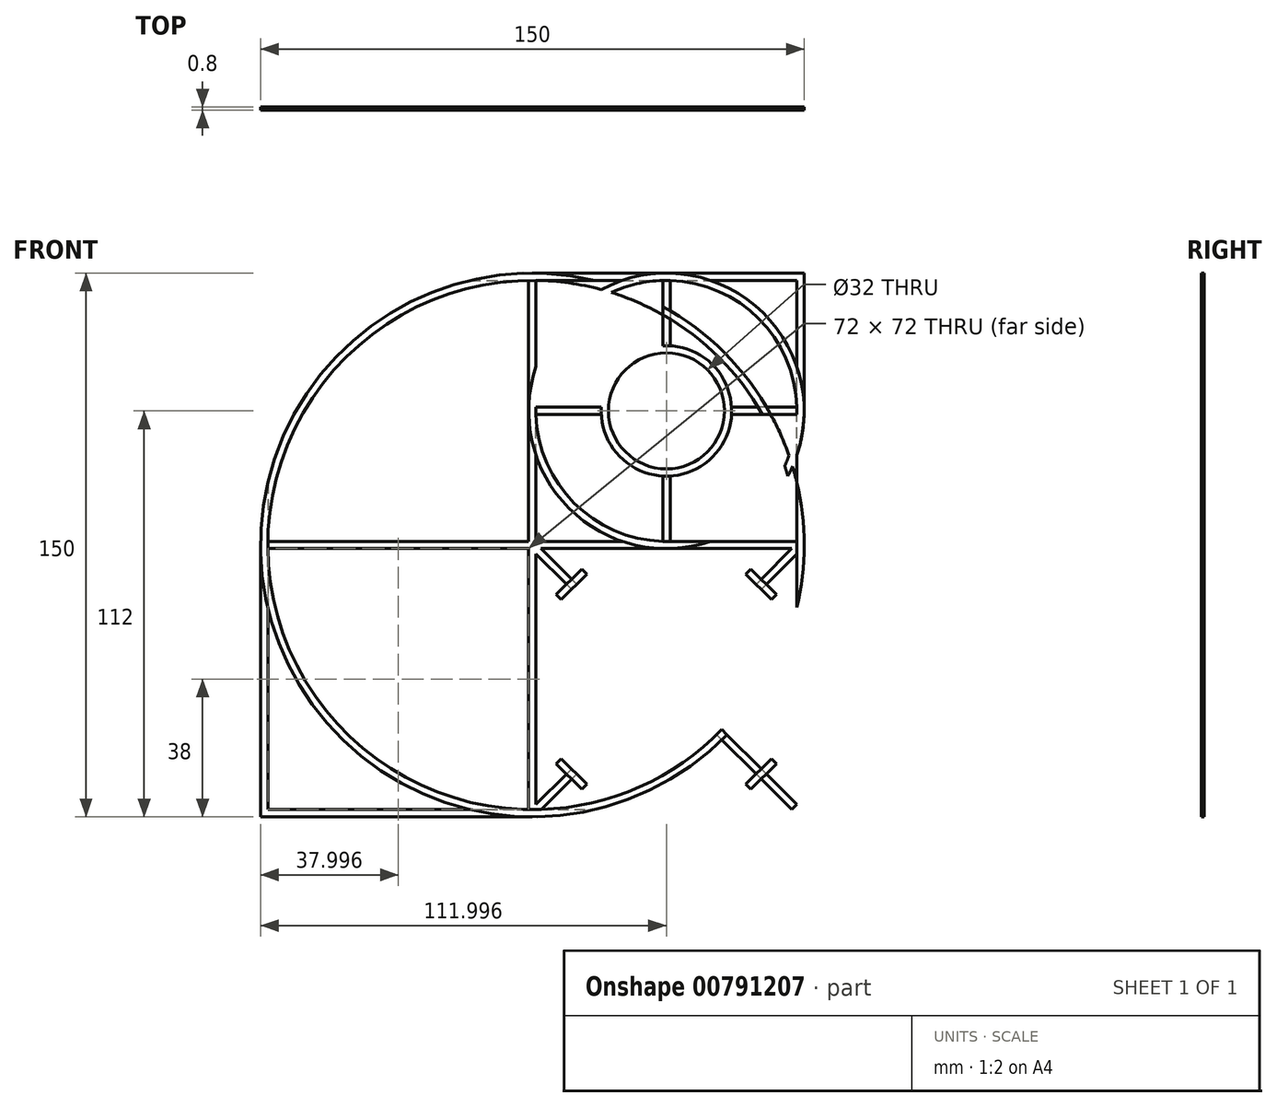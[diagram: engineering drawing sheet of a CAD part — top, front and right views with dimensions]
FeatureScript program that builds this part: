
annotation { "Feature Type Name" : "Feature", "Feature Type Description" : "" }
export const myFeature = defineFeature(function(context is Context, id is Id, definition is map)
    precondition{}
    {
        {
            var Q0;
            Q0=qCreatedBy(makeId("Front.planeOp"),FACE);
            var sketch = newSketch(context, id + "F0", { "sketchPlane" : qUnion([Q0])});
            skLineSegment(sketch, "E0.bottom", {"start": v(-75, 75.04) * mm, "end": v(75, 75.04) * mm});
            skLineSegment(sketch, "E0.top", {"start": v(-75, -74.96) * mm, "end": v(75, -74.96) * mm});
            skLineSegment(sketch, "E0.left", {"start": v(-75, 75.04) * mm, "end": v(-75, -74.96) * mm});
            skLineSegment(sketch, "E0.right", {"start": v(75, 75.04) * mm, "end": v(75, -74.96) * mm});
            skLineSegment(sketch, "E1.bottom", {"start": v(-73, 73.04) * mm, "end": v(-1, 73.04) * mm});
            skLineSegment(sketch, "E1.top", {"start": v(-73, -72.96) * mm, "end": v(-1, -72.96) * mm});
            skLineSegment(sketch, "E1.left", {"start": v(-73, 73.04) * mm, "end": v(-73, 1.04) * mm});
            skLineSegment(sketch, "E2.0", {"start": v(71.6, -0.96) * mm, "end": v(2.42, -0.96) * mm});
            skLineSegment(sketch, "E3.0", {"start": v(-1, 73.04) * mm, "end": v(-1, 1.04) * mm});
            skLineSegment(sketch, "E4.trimOffspring", {"start": v(-73, -0.96) * mm, "end": v(-73, -72.96) * mm});
            skLineSegment(sketch, "E5.trimOffspring", {"start": v(1, -2.37) * mm, "end": v(1, -71.55) * mm});
            skLineSegment(sketch, "E6.trimOffspring", {"start": v(-1, 1.04) * mm, "end": v(-73, 1.04) * mm});
            skLineSegment(sketch, "E7.trimOffspring", {"start": v(-1, -0.96) * mm, "end": v(-1, -72.96) * mm});
            skLineSegment(sketch, "E8.trimOffspring", {"start": v(-1, -0.96) * mm, "end": v(-73, -0.96) * mm});
            skLineSegment(sketch, "E9.trimOffspring", {"start": v(2.42, -72.96) * mm, "end": v(71.6, -72.96) * mm});
            skLineSegment(sketch, "E10.trimOffspring", {"start": v(73, -2.37) * mm, "end": v(73, -71.55) * mm});
            skLineSegment(sketch, "E11.0", {"start": v(1, -2.37) * mm, "end": v(35.6, -36.96) * mm});
            skLineSegment(sketch, "E12.0", {"start": v(2.42, -0.96) * mm, "end": v(37, -35.55) * mm});
            skLineSegment(sketch, "E13.trimOffspring", {"start": v(38.42, -36.96) * mm, "end": v(73, -71.55) * mm});
            skCircle(sketch, "E14", {"center": v(37, 37.04) * mm, "radius": 38 * mm});
            skCircle(sketch, "E15.0", {"center": v(37, 37.04) * mm, "radius": 36 * mm});
            skCircle(sketch, "E16", {"center": v(37, 37.04) * mm, "radius": 18 * mm});
            skCircle(sketch, "E17.0", {"center": v(37, 37.04) * mm, "radius": 16 * mm});
            skLineSegment(sketch, "E18.0", {"start": v(36, 73.04) * mm, "end": v(36, 55.01) * mm});
            skLineSegment(sketch, "E19.0", {"start": v(38, 73.04) * mm, "end": v(38, 55.01) * mm});
            skLineSegment(sketch, "E20.0", {"start": v(73, 38.04) * mm, "end": v(54.98, 38.04) * mm});
            skLineSegment(sketch, "E21.0", {"start": v(73, 36.04) * mm, "end": v(54.98, 36.04) * mm});
            skLineSegment(sketch, "E22.trimOffspring", {"start": v(36, 19.07) * mm, "end": v(36, 1.04) * mm});
            skLineSegment(sketch, "E23.trimOffspring", {"start": v(19.03, 38.04) * mm, "end": v(1, 38.04) * mm});
            skLineSegment(sketch, "E24.trimOffspring", {"start": v(38, 19.07) * mm, "end": v(38, 1.04) * mm});
            skLineSegment(sketch, "E25.trimOffspring", {"start": v(19.03, 36.04) * mm, "end": v(1, 36.04) * mm});
            skText(sketch, "E26", { "text": "36mm OD\n34mm ID", "fontName": "OpenSans-Bold.ttf"});
            skText(sketch, "E27", { "text": "76mm  OD\n72mm  ID", "fontName": "OpenSans-Bold.ttf"});
            skLineSegment(sketch, "E28", {"start": v(71.6, -72.96) * mm, "end": v(37, -38.37) * mm});
            skLineSegment(sketch, "E29", {"start": v(71.6, -0.96) * mm, "end": v(37, -35.55) * mm});
            skLineSegment(sketch, "E30", {"start": v(38.42, -36.96) * mm, "end": v(73, -2.37) * mm});
            skLineSegment(sketch, "E31", {"start": v(1, -71.55) * mm, "end": v(35.6, -36.96) * mm});
            skLineSegment(sketch, "E32", {"start": v(37, -38.37) * mm, "end": v(2.42, -72.96) * mm});
            skLineSegment(sketch, "E33", {"start": v(73, -2.37) * mm, "end": v(71.6, -0.96) * mm});
            skLineSegment(sketch, "E34", {"start": v(1, -71.55) * mm, "end": v(2.42, -72.96) * mm});
            skLineSegment(sketch, "E35", {"start": v(1, -2.37) * mm, "end": v(2.42, -0.96) * mm});
            skLineSegment(sketch, "E36", {"start": v(71.6, -72.96) * mm, "end": v(73, -71.55) * mm});
            skLineSegment(sketch, "E37", {"start": v(37, -35.55) * mm, "end": v(12.26, -10.8) * mm});
            skLineSegment(sketch, "E38", {"start": v(12.26, -10.8) * mm, "end": v(10.84, -12.21) * mm});
            skLineSegment(sketch, "E39", {"start": v(12.26, -10.8) * mm, "end": v(15.09, -7.97) * mm});
            skLineSegment(sketch, "E40", {"start": v(15.09, -7.97) * mm, "end": v(13.67, -6.55) * mm});
            skLineSegment(sketch, "E41", {"start": v(13.67, -6.55) * mm, "end": v(6.6, -13.63) * mm});
            skLineSegment(sketch, "E42", {"start": v(6.6, -13.63) * mm, "end": v(8.01, -15.04) * mm});
            skLineSegment(sketch, "E43", {"start": v(8.01, -15.04) * mm, "end": v(10.84, -12.21) * mm});
            skLineSegment(sketch, "E44", {"start": v(35.6, -36.96) * mm, "end": v(10.84, -61.7) * mm});
            skLineSegment(sketch, "E45", {"start": v(38.42, -36.96) * mm, "end": v(63.17, -61.7) * mm});
            skLineSegment(sketch, "E46", {"start": v(38.42, -36.96) * mm, "end": v(63.17, -12.21) * mm});
            skLineSegment(sketch, "E47", {"start": v(63.17, -12.21) * mm, "end": v(66, -15.04) * mm});
            skLineSegment(sketch, "E48", {"start": v(66, -15.04) * mm, "end": v(67.41, -13.63) * mm});
            skLineSegment(sketch, "E49", {"start": v(67.41, -13.63) * mm, "end": v(60.34, -6.55) * mm});
            skLineSegment(sketch, "E50", {"start": v(60.34, -6.55) * mm, "end": v(58.93, -7.97) * mm});
            skLineSegment(sketch, "E51", {"start": v(58.93, -7.97) * mm, "end": v(63.17, -12.21) * mm});
            skLineSegment(sketch, "E52", {"start": v(10.84, -61.7) * mm, "end": v(8.01, -58.88) * mm});
            skLineSegment(sketch, "E53", {"start": v(8.01, -58.88) * mm, "end": v(6.6, -60.3) * mm});
            skLineSegment(sketch, "E54", {"start": v(6.6, -60.3) * mm, "end": v(13.67, -67.37) * mm});
            skLineSegment(sketch, "E55", {"start": v(13.67, -67.37) * mm, "end": v(15.09, -65.95) * mm});
            skLineSegment(sketch, "E56", {"start": v(15.09, -65.95) * mm, "end": v(10.84, -61.7) * mm});
            skLineSegment(sketch, "E57", {"start": v(63.17, -61.7) * mm, "end": v(66, -58.88) * mm});
            skLineSegment(sketch, "E58", {"start": v(66, -58.88) * mm, "end": v(67.41, -60.3) * mm});
            skLineSegment(sketch, "E59", {"start": v(67.41, -60.3) * mm, "end": v(60.34, -67.37) * mm});
            skLineSegment(sketch, "E60", {"start": v(60.34, -67.37) * mm, "end": v(58.93, -65.95) * mm});
            skLineSegment(sketch, "E61", {"start": v(58.93, -65.95) * mm, "end": v(63.17, -61.7) * mm});
            skLineSegment(sketch, "E62", {"start": v(1, 1.04) * mm, "end": v(1, 73.04) * mm});
            skLineSegment(sketch, "E63", {"start": v(1, 73.04) * mm, "end": v(73, 73.04) * mm});
            skLineSegment(sketch, "E64", {"start": v(1, 1.04) * mm, "end": v(73, 1.04) * mm});
            skLineSegment(sketch, "E65", {"start": v(73, 1.04) * mm, "end": v(73, 73.04) * mm});
            skLineSegment(sketch, "E66", {"start": v(75, 75.04) * mm, "end": v(0, 75.04) * mm});
            skLineSegment(sketch, "E67", {"start": v(75, 75.04) * mm, "end": v(75, 0.04) * mm});
            skLineSegment(sketch, "E68", {"start": v(-75, -74.96) * mm, "end": v(0, -74.96) * mm});
            skCircle(sketch, "E69", {"center": v(0, 0.04) * mm, "radius": 75 * mm});
            skCircle(sketch, "E70.0", {"center": v(0, 0.04) * mm, "radius": 73 * mm});
            skText(sketch, "E71", { "text": "76mm  OD\n72mm  ID", "fontName": "OpenSans-Bold.ttf"});
            const initialGuessF0  = {"E26": [0.02316, 0.03863, 1, 0, 0.00397], "E27": [0.01856, 0.01389, 1, 0, 0.00397], "E71": [0.02468, -0.01252, 1, 0, 0.00397]};
            skSetInitialGuess(sketch, initialGuessF0);
            skSolve(sketch);
        }
        {
            var Q0;
            {var subQ0=sQuery(id+"F0.wireOp",EDGE,"E14");var subQ8=makeQuery(id+"F0.imprint","INTERSECT",VERTEX,{"derivedFrom":[sQuery(id+"F0.wireOp",EDGE,"E1.right"),subQ0]});Q0=makeQuery(id+"F0.imprint","IMPRINT",FACE,{"disambiguationData":[TD([[makeQuery(id+"F0.imprint","IMPRINT",EDGE,{"disambiguationData":[TD([[subQ8,1.0]])],"derivedFrom":subQ0}),1.0]])]});}
            var Q1;
            Q1=makeQuery(id+"F0.imprint","IMPRINT",FACE,{"disambiguationData":[TD([[makeQuery(id+"F0.imprint","IMPRINT",EDGE,{"derivedFrom":sQuery(id+"F0.wireOp",EDGE,"E17.0")}),-1.0]])]});
            var Q2;
            {var subQ0=sQuery(id+"F0.wireOp",EDGE,"E65");var subQ9=sQuery(id+"F0.wireOp",EDGE,"E14");var subQ10=makeQuery(id+"F0.imprint","INTERSECT",VERTEX,{"disambiguationData":[OD(0.0)],"derivedFrom":[subQ9,subQ0]});Q2=makeQuery(id+"F0.imprint","IMPRINT",FACE,{"disambiguationData":[TD([[makeQuery(id+"F0.imprint","IMPRINT",EDGE,{"disambiguationData":[TD([[subQ10,-1.0]])],"derivedFrom":subQ9}),1.0]])]});}
            var Q3;
            {var subQ0=sQuery(id+"F0.wireOp",EDGE,"E63");var subQ9=sQuery(id+"F0.wireOp",EDGE,"E14");var subQ10=makeQuery(id+"F0.imprint","INTERSECT",VERTEX,{"disambiguationData":[OD(1.0)],"derivedFrom":[subQ9,subQ0]});Q3=makeQuery(id+"F0.imprint","IMPRINT",FACE,{"disambiguationData":[TD([[makeQuery(id+"F0.imprint","IMPRINT",EDGE,{"disambiguationData":[TD([[subQ10,-1.0]])],"derivedFrom":subQ9}),1.0]])]});}
            var Q4;
            {var subQ0=sQuery(id+"F0.wireOp",EDGE,"E62");var subQ9=sQuery(id+"F0.wireOp",EDGE,"E14");var subQ10=makeQuery(id+"F0.imprint","INTERSECT",VERTEX,{"disambiguationData":[OD(1.0)],"derivedFrom":[subQ9,subQ0]});Q4=makeQuery(id+"F0.imprint","IMPRINT",FACE,{"disambiguationData":[TD([[makeQuery(id+"F0.imprint","IMPRINT",EDGE,{"disambiguationData":[TD([[subQ10,-1.0]])],"derivedFrom":subQ9}),1.0]])]});}
            var Q5;
            {var subQ0=sQuery(id+"F0.wireOp",EDGE,"E64");var subQ9=sQuery(id+"F0.wireOp",EDGE,"E14");var subQ11=makeQuery(id+"F0.imprint","INTERSECT",VERTEX,{"disambiguationData":[OD(1.0)],"derivedFrom":[subQ9,subQ0]});Q5=makeQuery(id+"F0.imprint","IMPRINT",FACE,{"disambiguationData":[TD([[makeQuery(id+"F0.imprint","IMPRINT",EDGE,{"disambiguationData":[TD([[subQ11,-1.0]])],"derivedFrom":subQ9}),1.0]])]});}
            var Q6;
            {var subQ4=sQuery(id+"F0.wireOp",EDGE,"E42");Q6=makeQuery(id+"F0.imprint","IMPRINT",FACE,{"disambiguationData":[TD([[makeQuery(id+"F0.imprint","IMPRINT",EDGE,{"derivedFrom":subQ4}),1.0]])]});}
            var Q7;
            {var subQ0=sQuery(id+"F0.wireOp",EDGE,"E39");Q7=makeQuery(id+"F0.imprint","IMPRINT",FACE,{"disambiguationData":[TD([[makeQuery(id+"F0.imprint","IMPRINT",EDGE,{"derivedFrom":subQ0}),1.0]])]});}
            var Q8;
            {var subQ0=sQuery(id+"F0.wireOp",EDGE,"E38");Q8=makeQuery(id+"F0.imprint","IMPRINT",FACE,{"disambiguationData":[TD([[makeQuery(id+"F0.imprint","IMPRINT",EDGE,{"derivedFrom":subQ0}),-1.0]])]});}
            var Q9;
            {var subQ0=sQuery(id+"F0.wireOp",EDGE,"E47");Q9=makeQuery(id+"F0.imprint","IMPRINT",FACE,{"disambiguationData":[TD([[makeQuery(id+"F0.imprint","IMPRINT",EDGE,{"derivedFrom":subQ0}),1.0]])]});}
            var Q10;
            {var subQ5=sQuery(id+"F0.wireOp",EDGE,"E50");Q10=makeQuery(id+"F0.imprint","IMPRINT",FACE,{"disambiguationData":[TD([[makeQuery(id+"F0.imprint","IMPRINT",EDGE,{"derivedFrom":subQ5}),1.0]])]});}
            var Q11;
            {var subQ0=sQuery(id+"F0.wireOp",EDGE,"E49");var subQ1=sQuery(id+"F0.wireOp",EDGE,"E29");var subQ2=makeQuery(id+"F0.imprint","INTERSECT",VERTEX,{"derivedFrom":[subQ1,subQ0]});Q11=makeQuery(id+"F0.imprint","IMPRINT",FACE,{"disambiguationData":[TD([[makeQuery(id+"F0.imprint","IMPRINT",EDGE,{"disambiguationData":[TD([[subQ2,-1.0]])],"derivedFrom":subQ1}),1.0]])]});}
            var Q12;
            {var subQ5=sQuery(id+"F0.wireOp",EDGE,"E55");Q12=makeQuery(id+"F0.imprint","IMPRINT",FACE,{"disambiguationData":[TD([[makeQuery(id+"F0.imprint","IMPRINT",EDGE,{"derivedFrom":subQ5}),1.0]])]});}
            var Q13;
            {var subQ0=sQuery(id+"F0.wireOp",EDGE,"E52");Q13=makeQuery(id+"F0.imprint","IMPRINT",FACE,{"disambiguationData":[TD([[makeQuery(id+"F0.imprint","IMPRINT",EDGE,{"derivedFrom":subQ0}),1.0]])]});}
            var Q14;
            {var subQ0=sQuery(id+"F0.wireOp",EDGE,"E56");var subQ5=sQuery(id+"F0.wireOp",EDGE,"E32");var subQ6=makeQuery(id+"F0.imprint","INTERSECT",VERTEX,{"derivedFrom":[subQ5,subQ0]});Q14=makeQuery(id+"F0.imprint","IMPRINT",FACE,{"disambiguationData":[TD([[makeQuery(id+"F0.imprint","IMPRINT",EDGE,{"disambiguationData":[TD([[subQ6,-1.0]])],"derivedFrom":subQ5}),-1.0]])]});}
            var Q15;
            {var subQ3=sQuery(id+"F0.wireOp",EDGE,"E59");var subQ5=sQuery(id+"F0.wireOp",EDGE,"E28");var subQ6=makeQuery(id+"F0.imprint","INTERSECT",VERTEX,{"derivedFrom":[subQ5,subQ3]});Q15=makeQuery(id+"F0.imprint","IMPRINT",FACE,{"disambiguationData":[TD([[makeQuery(id+"F0.imprint","IMPRINT",EDGE,{"disambiguationData":[TD([[subQ6,-1.0]])],"derivedFrom":subQ5}),-1.0]])]});}
            var Q16;
            {var subQ0=sQuery(id+"F0.wireOp",EDGE,"E57");Q16=makeQuery(id+"F0.imprint","IMPRINT",FACE,{"disambiguationData":[TD([[makeQuery(id+"F0.imprint","IMPRINT",EDGE,{"derivedFrom":subQ0}),-1.0]])]});}
            var Q17;
            {var subQ5=sQuery(id+"F0.wireOp",EDGE,"E60");Q17=makeQuery(id+"F0.imprint","IMPRINT",FACE,{"disambiguationData":[TD([[makeQuery(id+"F0.imprint","IMPRINT",EDGE,{"derivedFrom":subQ5}),-1.0]])]});}
            var Q18;
            {var subQ3=sQuery(id+"F0.wireOp",EDGE,"E14");var subQ7=sQuery(id+"F0.wireOp",EDGE,"E70.0");var subQ9=makeQuery(id+"F0.imprint","INTERSECT",VERTEX,{"disambiguationData":[OD(0.0)],"derivedFrom":[subQ3,subQ7]});Q18=makeQuery(id+"F0.imprint","IMPRINT",FACE,{"disambiguationData":[TD([[makeQuery(id+"F0.imprint","IMPRINT",EDGE,{"disambiguationData":[TD([[subQ9,-1.0]])],"derivedFrom":subQ3}),1.0]])]});}
            var Q19;
            {var subQ0=sQuery(id+"F0.wireOp",EDGE,"E69");var subQ1=sQuery(id+"F0.wireOp",EDGE,"E14");var subQ2=makeQuery(id+"F0.imprint","INTERSECT",VERTEX,{"disambiguationData":[OD(0.0)],"derivedFrom":[subQ1,subQ0]});Q19=makeQuery(id+"F0.imprint","IMPRINT",FACE,{"disambiguationData":[TD([[makeQuery(id+"F0.imprint","IMPRINT",EDGE,{"disambiguationData":[TD([[subQ2,-1.0]])],"derivedFrom":subQ1}),-1.0]])]});}
            var Q20;
            {var subQ0=sQuery(id+"F0.wireOp",EDGE,"E69");var subQ1=sQuery(id+"F0.wireOp",EDGE,"E15.0");var subQ2=makeQuery(id+"F0.imprint","INTERSECT",VERTEX,{"disambiguationData":[OD(0.0)],"derivedFrom":[subQ1,subQ0]});Q20=makeQuery(id+"F0.imprint","IMPRINT",FACE,{"disambiguationData":[TD([[makeQuery(id+"F0.imprint","IMPRINT",EDGE,{"disambiguationData":[TD([[subQ2,-1.0]])],"derivedFrom":subQ1}),1.0]])]});}
            var Q21;
            {var subQ0=sQuery(id+"F0.wireOp",EDGE,"E69");var subQ1=sQuery(id+"F0.wireOp",EDGE,"E18.0");var subQ2=makeQuery(id+"F0.imprint","INTERSECT",VERTEX,{"derivedFrom":[subQ1,subQ0]});Q21=makeQuery(id+"F0.imprint","IMPRINT",FACE,{"disambiguationData":[TD([[makeQuery(id+"F0.imprint","IMPRINT",EDGE,{"disambiguationData":[TD([[subQ2,-1.0]])],"derivedFrom":subQ1}),1.0]])]});}
            var Q22;
            {var subQ0=sQuery(id+"F0.wireOp",EDGE,"E69");var subQ1=sQuery(id+"F0.wireOp",EDGE,"E19.0");var subQ2=makeQuery(id+"F0.imprint","INTERSECT",VERTEX,{"derivedFrom":[subQ1,subQ0]});Q22=makeQuery(id+"F0.imprint","IMPRINT",FACE,{"disambiguationData":[TD([[makeQuery(id+"F0.imprint","IMPRINT",EDGE,{"disambiguationData":[TD([[subQ2,-1.0]])],"derivedFrom":subQ1}),1.0]])]});}
            var Q23;
            {var subQ0=sQuery(id+"F0.wireOp",EDGE,"E70.0");var subQ1=sQuery(id+"F0.wireOp",EDGE,"E15.0");var subQ2=makeQuery(id+"F0.imprint","INTERSECT",VERTEX,{"disambiguationData":[OD(1.0)],"derivedFrom":[subQ1,subQ0]});Q23=makeQuery(id+"F0.imprint","IMPRINT",FACE,{"disambiguationData":[TD([[makeQuery(id+"F0.imprint","IMPRINT",EDGE,{"disambiguationData":[TD([[subQ2,-1.0]])],"derivedFrom":subQ1}),1.0]])]});}
            var Q24;
            {var subQ0=sQuery(id+"F0.wireOp",EDGE,"E69");var subQ1=sQuery(id+"F0.wireOp",EDGE,"E20.0");var subQ2=makeQuery(id+"F0.imprint","INTERSECT",VERTEX,{"derivedFrom":[subQ1,subQ0]});Q24=makeQuery(id+"F0.imprint","IMPRINT",FACE,{"disambiguationData":[TD([[makeQuery(id+"F0.imprint","IMPRINT",EDGE,{"disambiguationData":[TD([[subQ2,-1.0]])],"derivedFrom":subQ1}),1.0]])]});}
            var Q25;
            {var subQ0=sQuery(id+"F0.wireOp",EDGE,"E70.0");var subQ1=sQuery(id+"F0.wireOp",EDGE,"E14");var subQ2=makeQuery(id+"F0.imprint","INTERSECT",VERTEX,{"disambiguationData":[OD(1.0)],"derivedFrom":[subQ1,subQ0]});Q25=makeQuery(id+"F0.imprint","IMPRINT",FACE,{"disambiguationData":[TD([[makeQuery(id+"F0.imprint","IMPRINT",EDGE,{"disambiguationData":[TD([[subQ2,-1.0]])],"derivedFrom":subQ1}),1.0]])]});}
            var Q26;
            {var subQ5=sQuery(id+"F0.wireOp",EDGE,"E70.0");var subQ7=sQuery(id+"F0.wireOp",EDGE,"E14");var subQ9=makeQuery(id+"F0.imprint","INTERSECT",VERTEX,{"disambiguationData":[OD(1.0)],"derivedFrom":[subQ7,subQ5]});Q26=makeQuery(id+"F0.imprint","IMPRINT",FACE,{"disambiguationData":[TD([[makeQuery(id+"F0.imprint","IMPRINT",EDGE,{"disambiguationData":[TD([[subQ9,-1.0]])],"derivedFrom":subQ7}),-1.0]])]});}
            var Q27;
            {var subQ3=sQuery(id+"F0.wireOp",EDGE,"E45");var subQ5=sQuery(id+"F0.wireOp",EDGE,"E70.0");var subQ6=makeQuery(id+"F0.imprint","INTERSECT",VERTEX,{"derivedFrom":[subQ3,subQ5]});Q27=makeQuery(id+"F0.imprint","IMPRINT",FACE,{"disambiguationData":[TD([[makeQuery(id+"F0.imprint","IMPRINT",EDGE,{"disambiguationData":[TD([[subQ6,-1.0]])],"derivedFrom":subQ3}),1.0]])]});}
            var Q28;
            {var subQ0=sQuery(id+"F0.wireOp",EDGE,"E65");var subQ1=sQuery(id+"F0.wireOp",EDGE,"E64");var subQ2=makeQuery(id+"F0.imprint","INTERSECT",VERTEX,{"derivedFrom":[subQ1,subQ0]});Q28=makeQuery(id+"F0.imprint","IMPRINT",FACE,{"disambiguationData":[TD([[makeQuery(id+"F0.imprint","IMPRINT",EDGE,{"disambiguationData":[TD([[subQ2,1.0]])],"derivedFrom":subQ1}),-1.0]])]});}
            var Q29;
            {var subQ0=sQuery(id+"F0.wireOp",EDGE,"E69");var subQ3=sQuery(id+"F0.wireOp",EDGE,"E28");var subQ4=makeQuery(id+"F0.imprint","INTERSECT",VERTEX,{"derivedFrom":[subQ3,subQ0]});Q29=makeQuery(id+"F0.imprint","IMPRINT",FACE,{"disambiguationData":[TD([[makeQuery(id+"F0.imprint","IMPRINT",EDGE,{"disambiguationData":[TD([[subQ4,-1.0]])],"derivedFrom":subQ3}),1.0]])]});}
            var Q30;
            {var subQ0=sQuery(id+"F0.wireOp",EDGE,"E69");var subQ1=sQuery(id+"F0.wireOp",EDGE,"E28");var subQ2=makeQuery(id+"F0.imprint","INTERSECT",VERTEX,{"derivedFrom":[subQ1,subQ0]});Q30=makeQuery(id+"F0.imprint","IMPRINT",FACE,{"disambiguationData":[TD([[makeQuery(id+"F0.imprint","IMPRINT",EDGE,{"disambiguationData":[TD([[subQ2,-1.0]])],"derivedFrom":subQ1}),-1.0]])]});}
            var Q31;
            {var subQ5=sQuery(id+"F0.wireOp",EDGE,"E7.trimOffspring");var subQ6=sQuery(id+"F0.wireOp",EDGE,"E1.top");var subQ7=makeQuery(id+"F0.imprint","INTERSECT",VERTEX,{"derivedFrom":[subQ6,subQ5]});Q31=makeQuery(id+"F0.imprint","IMPRINT",FACE,{"disambiguationData":[TD([[makeQuery(id+"F0.imprint","IMPRINT",EDGE,{"disambiguationData":[TD([[subQ7,1.0]])],"derivedFrom":subQ6}),1.0]])]});}
            var Q32;
            {var subQ7=sQuery(id+"F0.wireOp",EDGE,"E7.trimOffspring");var subQ8=sQuery(id+"F0.wireOp",EDGE,"E1.top");var subQ9=makeQuery(id+"F0.imprint","INTERSECT",VERTEX,{"derivedFrom":[subQ8,subQ7]});Q32=makeQuery(id+"F0.imprint","IMPRINT",FACE,{"disambiguationData":[TD([[makeQuery(id+"F0.imprint","IMPRINT",EDGE,{"disambiguationData":[TD([[subQ9,1.0]])],"derivedFrom":subQ8}),-1.0]])]});}
            var Q33;
            {var subQ0=sQuery(id+"F0.wireOp",EDGE,"E3.0");var subQ1=sQuery(id+"F0.wireOp",EDGE,"E1.bottom");var subQ2=makeQuery(id+"F0.imprint","INTERSECT",VERTEX,{"derivedFrom":[subQ1,subQ0]});Q33=makeQuery(id+"F0.imprint","IMPRINT",FACE,{"disambiguationData":[TD([[makeQuery(id+"F0.imprint","IMPRINT",EDGE,{"disambiguationData":[TD([[subQ2,1.0]])],"derivedFrom":subQ1}),-1.0]])]});}
            var Q34;
            {var subQ8=sQuery(id+"F0.wireOp",EDGE,"E1.left");var subQ10=sQuery(id+"F0.wireOp",EDGE,"E6.trimOffspring");var subQ11=makeQuery(id+"F0.imprint","INTERSECT",VERTEX,{"derivedFrom":[subQ8,subQ10]});Q34=makeQuery(id+"F0.imprint","IMPRINT",FACE,{"disambiguationData":[TD([[makeQuery(id+"F0.imprint","IMPRINT",EDGE,{"disambiguationData":[TD([[subQ11,1.0]])],"derivedFrom":subQ8}),-1.0]])]});}
            var Q35;
            {var subQ5=sQuery(id+"F0.wireOp",EDGE,"E3.0");var subQ6=sQuery(id+"F0.wireOp",EDGE,"E1.bottom");var subQ7=makeQuery(id+"F0.imprint","INTERSECT",VERTEX,{"derivedFrom":[subQ6,subQ5]});Q35=makeQuery(id+"F0.imprint","IMPRINT",FACE,{"disambiguationData":[TD([[makeQuery(id+"F0.imprint","IMPRINT",EDGE,{"disambiguationData":[TD([[subQ7,1.0]])],"derivedFrom":subQ6}),1.0]])]});}
            var Q36;
            {var subQ0=sQuery(id+"F0.wireOp",EDGE,"E69");var subQ1=sQuery(id+"F0.wireOp",EDGE,"E14");var subQ2=makeQuery(id+"F0.imprint","INTERSECT",VERTEX,{"disambiguationData":[OD(0.0)],"derivedFrom":[subQ1,subQ0]});Q36=makeQuery(id+"F0.imprint","IMPRINT",FACE,{"disambiguationData":[TD([[makeQuery(id+"F0.imprint","IMPRINT",EDGE,{"disambiguationData":[TD([[subQ2,-1.0]])],"derivedFrom":subQ1}),1.0]])]});}
            var Q37;
            {var subQ3=sQuery(id+"F0.wireOp",EDGE,"E14");var subQ7=sQuery(id+"F0.wireOp",EDGE,"E69");var subQ9=makeQuery(id+"F0.imprint","INTERSECT",VERTEX,{"disambiguationData":[OD(1.0)],"derivedFrom":[subQ3,subQ7]});Q37=makeQuery(id+"F0.imprint","IMPRINT",FACE,{"disambiguationData":[TD([[makeQuery(id+"F0.imprint","IMPRINT",EDGE,{"disambiguationData":[TD([[subQ9,-1.0]])],"derivedFrom":subQ3}),1.0]])]});}
            extrude(context, id + "F1", {"entities" : qUnion([Q0, Q1, Q2, Q3, Q4, Q5, Q6, Q7, Q8, Q9, Q10, Q11, Q12, Q13, Q14, Q15, Q16, Q17, Q18, Q19, Q20, Q21, Q22, Q23, Q24, Q25, Q26, Q27, Q28, Q29, Q30, Q31, Q32, Q33, Q34, Q35, Q36, Q37]), "depth" : .8 * mm, "offsetDistance" : 25 * mm});
        }
        {
            var Q0;
            {var subQ7=sQuery(id+"F0.wireOp",EDGE,"E0.top");Q0=makeQuery(id+"F0.imprint","IMPRINT",FACE,{"disambiguationData":[TD([[makeQuery(id+"F0.imprint","IMPRINT",EDGE,{"derivedFrom":subQ7}),1.0]])]});}
            var Q1;
            {var subQ6=sQuery(id+"F0.wireOp",EDGE,"E0.bottom");Q1=makeQuery(id+"F0.imprint","IMPRINT",FACE,{"disambiguationData":[TD([[makeQuery(id+"F0.imprint","IMPRINT",EDGE,{"derivedFrom":subQ6}),-1.0]])]});}
            var Q2;
            {var subQ0=sQuery(id+"F0.wireOp",EDGE,"E23.trimOffspring");var subQ5=sQuery(id+"F0.wireOp",EDGE,"E15.0");var subQ8=makeQuery(id+"F0.imprint","INTERSECT",VERTEX,{"derivedFrom":[subQ5,subQ0]});Q2=makeQuery(id+"F0.imprint","IMPRINT",FACE,{"disambiguationData":[TD([[makeQuery(id+"F0.imprint","IMPRINT",EDGE,{"disambiguationData":[TD([[subQ8,-1.0]])],"derivedFrom":subQ5}),1.0]])]});}
            var Q3;
            {var subQ0=sQuery(id+"F0.wireOp",EDGE,"E22.trimOffspring");var subQ3=sQuery(id+"F0.wireOp",EDGE,"E15.0");var subQ4=makeQuery(id+"F0.imprint","INTERSECT",VERTEX,{"derivedFrom":[subQ3,subQ0]});Q3=makeQuery(id+"F0.imprint","IMPRINT",FACE,{"disambiguationData":[TD([[makeQuery(id+"F0.imprint","IMPRINT",EDGE,{"disambiguationData":[TD([[subQ4,-1.0]])],"derivedFrom":subQ3}),1.0]])]});}
            var Q4;
            {var subQ0=sQuery(id+"F0.wireOp",EDGE,"E19.0");var subQ1=sQuery(id+"F0.wireOp",EDGE,"E15.0");var subQ2=makeQuery(id+"F0.imprint","INTERSECT",VERTEX,{"derivedFrom":[subQ1,subQ0]});Q4=makeQuery(id+"F0.imprint","IMPRINT",FACE,{"disambiguationData":[TD([[makeQuery(id+"F0.imprint","IMPRINT",EDGE,{"disambiguationData":[TD([[subQ2,-1.0]])],"derivedFrom":subQ1}),1.0]])]});}
            var Q5;
            {var subQ1=sQuery(id+"F0.wireOp",EDGE,"E15.0");var subQ5=sQuery(id+"F0.wireOp",EDGE,"E20.0");var subQ6=makeQuery(id+"F0.imprint","INTERSECT",VERTEX,{"derivedFrom":[subQ1,subQ5]});Q5=makeQuery(id+"F0.imprint","IMPRINT",FACE,{"disambiguationData":[TD([[makeQuery(id+"F0.imprint","IMPRINT",EDGE,{"disambiguationData":[TD([[subQ6,1.0]])],"derivedFrom":subQ1}),1.0]])]});}
            var Q6;
            {var subQ0=sQuery(id+"F0.wireOp",EDGE,"E35");Q6=makeQuery(id+"F0.imprint","IMPRINT",FACE,{"disambiguationData":[TD([[makeQuery(id+"F0.imprint","IMPRINT",EDGE,{"derivedFrom":subQ0}),-1.0]])]});}
            var Q7;
            {var subQ13=sQuery(id+"F0.wireOp",EDGE,"E37");Q7=makeQuery(id+"F0.imprint","IMPRINT",FACE,{"disambiguationData":[TD([[makeQuery(id+"F0.imprint","IMPRINT",EDGE,{"derivedFrom":subQ13}),1.0]])]});}
            var Q8;
            {var subQ1=sQuery(id+"F0.wireOp",EDGE,"E30");var subQ3=sQuery(id+"F0.wireOp",EDGE,"E70.0");var subQ4=makeQuery(id+"F0.imprint","INTERSECT",VERTEX,{"derivedFrom":[subQ1,subQ3]});Q8=makeQuery(id+"F0.imprint","IMPRINT",FACE,{"disambiguationData":[TD([[makeQuery(id+"F0.imprint","IMPRINT",EDGE,{"disambiguationData":[TD([[subQ4,-1.0]])],"derivedFrom":subQ3}),-1.0]])]});}
            var Q9;
            {var subQ0=sQuery(id+"F0.wireOp",EDGE,"E36");Q9=makeQuery(id+"F0.imprint","IMPRINT",FACE,{"disambiguationData":[TD([[makeQuery(id+"F0.imprint","IMPRINT",EDGE,{"derivedFrom":subQ0}),1.0]])]});}
            var Q10;
            {var subQ1=sQuery(id+"F0.wireOp",EDGE,"E32");var subQ3=sQuery(id+"F0.wireOp",EDGE,"E70.0");var subQ4=makeQuery(id+"F0.imprint","INTERSECT",VERTEX,{"derivedFrom":[subQ1,subQ3]});Q10=makeQuery(id+"F0.imprint","IMPRINT",FACE,{"disambiguationData":[TD([[makeQuery(id+"F0.imprint","IMPRINT",EDGE,{"disambiguationData":[TD([[subQ4,1.0]])],"derivedFrom":subQ3}),-1.0]])]});}
            var Q11;
            {var subQ0=sQuery(id+"F0.wireOp",EDGE,"E61");var subQ1=sQuery(id+"F0.wireOp",EDGE,"E28");var subQ2=makeQuery(id+"F0.imprint","INTERSECT",VERTEX,{"derivedFrom":[subQ1,subQ0]});Q11=makeQuery(id+"F0.imprint","IMPRINT",FACE,{"disambiguationData":[TD([[makeQuery(id+"F0.imprint","IMPRINT",EDGE,{"disambiguationData":[TD([[subQ2,-1.0]])],"derivedFrom":subQ1}),-1.0]])]});}
            var Q12;
            {var subQ0=sQuery(id+"F0.wireOp",EDGE,"E69");var subQ1=sQuery(id+"F0.wireOp",EDGE,"E28");var subQ2=makeQuery(id+"F0.imprint","INTERSECT",VERTEX,{"derivedFrom":[subQ1,subQ0]});Q12=makeQuery(id+"F0.imprint","IMPRINT",FACE,{"disambiguationData":[TD([[makeQuery(id+"F0.imprint","IMPRINT",EDGE,{"disambiguationData":[TD([[subQ2,-1.0]])],"derivedFrom":subQ1}),-1.0]])]});}
            var Q13;
            {var subQ0=sQuery(id+"F0.wireOp",EDGE,"E20.0");var subQ1=sQuery(id+"F0.wireOp",EDGE,"E16");var subQ2=makeQuery(id+"F0.imprint","INTERSECT",VERTEX,{"derivedFrom":[subQ1,subQ0]});Q13=makeQuery(id+"F0.imprint","IMPRINT",FACE,{"disambiguationData":[TD([[makeQuery(id+"F0.imprint","IMPRINT",EDGE,{"disambiguationData":[TD([[subQ2,1.0]])],"derivedFrom":subQ1}),-1.0]])]});}
            var Q14;
            {var subQ0=sQuery(id+"F0.wireOp",EDGE,"E69");var subQ1=sQuery(id+"F0.wireOp",EDGE,"E20.0");var subQ2=makeQuery(id+"F0.imprint","INTERSECT",VERTEX,{"derivedFrom":[subQ1,subQ0]});Q14=makeQuery(id+"F0.imprint","IMPRINT",FACE,{"disambiguationData":[TD([[makeQuery(id+"F0.imprint","IMPRINT",EDGE,{"disambiguationData":[TD([[subQ2,-1.0]])],"derivedFrom":subQ1}),1.0]])]});}
            var Q15;
            {var subQ0=sQuery(id+"F0.wireOp",EDGE,"E69");var subQ1=sQuery(id+"F0.wireOp",EDGE,"E18.0");var subQ2=makeQuery(id+"F0.imprint","INTERSECT",VERTEX,{"derivedFrom":[subQ1,subQ0]});Q15=makeQuery(id+"F0.imprint","IMPRINT",FACE,{"disambiguationData":[TD([[makeQuery(id+"F0.imprint","IMPRINT",EDGE,{"disambiguationData":[TD([[subQ2,-1.0]])],"derivedFrom":subQ1}),1.0]])]});}
            var Q16;
            {var subQ0=sQuery(id+"F0.wireOp",EDGE,"E18.0");var subQ1=sQuery(id+"F0.wireOp",EDGE,"E16");var subQ2=makeQuery(id+"F0.imprint","INTERSECT",VERTEX,{"derivedFrom":[subQ1,subQ0]});Q16=makeQuery(id+"F0.imprint","IMPRINT",FACE,{"disambiguationData":[TD([[makeQuery(id+"F0.imprint","IMPRINT",EDGE,{"disambiguationData":[TD([[subQ2,1.0]])],"derivedFrom":subQ1}),-1.0]])]});}
            var Q17;
            {var subQ0=sQuery(id+"F0.wireOp",EDGE,"E66");var subQ1=sQuery(id+"F0.wireOp",EDGE,"E14");var subQ2=makeQuery(id+"F0.imprint","INTERSECT",VERTEX,{"derivedFrom":[subQ1,subQ0]});Q17=makeQuery(id+"F0.imprint","IMPRINT",FACE,{"disambiguationData":[TD([[makeQuery(id+"F0.imprint","IMPRINT",EDGE,{"disambiguationData":[TD([[subQ2,-1.0]])],"derivedFrom":subQ1}),-1.0]])]});}
            var Q18;
            {var subQ3=sQuery(id+"F0.wireOp",EDGE,"E14");var subQ8=sQuery(id+"F0.wireOp",EDGE,"E67");var subQ9=makeQuery(id+"F0.imprint","INTERSECT",VERTEX,{"derivedFrom":[subQ3,subQ8]});Q18=makeQuery(id+"F0.imprint","IMPRINT",FACE,{"disambiguationData":[TD([[makeQuery(id+"F0.imprint","IMPRINT",EDGE,{"disambiguationData":[TD([[subQ9,-1.0]])],"derivedFrom":subQ3}),-1.0]])]});}
            var Q19;
            {var subQ0=sQuery(id+"F0.wireOp",EDGE,"E67");var subQ1=sQuery(id+"F0.wireOp",EDGE,"E14");var subQ2=makeQuery(id+"F0.imprint","INTERSECT",VERTEX,{"derivedFrom":[subQ1,subQ0]});Q19=makeQuery(id+"F0.imprint","IMPRINT",FACE,{"disambiguationData":[TD([[makeQuery(id+"F0.imprint","IMPRINT",EDGE,{"disambiguationData":[TD([[subQ2,1.0]])],"derivedFrom":subQ1}),-1.0]])]});}
            var Q20;
            {var subQ0=sQuery(id+"F0.wireOp",EDGE,"E65");var subQ1=sQuery(id+"F0.wireOp",EDGE,"E64");var subQ2=makeQuery(id+"F0.imprint","INTERSECT",VERTEX,{"derivedFrom":[subQ1,subQ0]});Q20=makeQuery(id+"F0.imprint","IMPRINT",FACE,{"disambiguationData":[TD([[makeQuery(id+"F0.imprint","IMPRINT",EDGE,{"disambiguationData":[TD([[subQ2,1.0]])],"derivedFrom":subQ1}),-1.0]])]});}
            var Q21;
            {var subQ3=sQuery(id+"F0.wireOp",EDGE,"E14");var subQ5=makeQuery(id+"F0.imprint","INTERSECT",VERTEX,{"derivedFrom":[subQ3,sQuery(id+"F0.wireOp",EDGE,"E67")]});Q21=makeQuery(id+"F0.imprint","IMPRINT",FACE,{"disambiguationData":[TD([[makeQuery(id+"F0.imprint","IMPRINT",EDGE,{"disambiguationData":[TD([[subQ5,-1.0]])],"derivedFrom":subQ3}),1.0]])]});}
            var Q22;
            {var subQ3=sQuery(id+"F0.wireOp",EDGE,"E14");var subQ5=makeQuery(id+"F0.imprint","INTERSECT",VERTEX,{"derivedFrom":[subQ3,sQuery(id+"F0.wireOp",EDGE,"E66")]});Q22=makeQuery(id+"F0.imprint","IMPRINT",FACE,{"disambiguationData":[TD([[makeQuery(id+"F0.imprint","IMPRINT",EDGE,{"disambiguationData":[TD([[subQ5,1.0]])],"derivedFrom":subQ3}),1.0]])]});}
            var Q23;
            {var subQ5=sQuery(id+"F0.wireOp",EDGE,"E3.0");var subQ6=sQuery(id+"F0.wireOp",EDGE,"E1.bottom");var subQ7=makeQuery(id+"F0.imprint","INTERSECT",VERTEX,{"derivedFrom":[subQ6,subQ5]});Q23=makeQuery(id+"F0.imprint","IMPRINT",FACE,{"disambiguationData":[TD([[makeQuery(id+"F0.imprint","IMPRINT",EDGE,{"disambiguationData":[TD([[subQ7,1.0]])],"derivedFrom":subQ6}),1.0]])]});}
            var Q24;
            {var subQ0=sQuery(id+"F0.wireOp",EDGE,"E70.0");var subQ1=sQuery(id+"F0.wireOp",EDGE,"E3.0");var subQ2=makeQuery(id+"F0.imprint","INTERSECT",VERTEX,{"derivedFrom":[subQ1,subQ0]});Q24=makeQuery(id+"F0.imprint","IMPRINT",FACE,{"disambiguationData":[TD([[makeQuery(id+"F0.imprint","IMPRINT",EDGE,{"disambiguationData":[TD([[subQ2,-1.0]])],"derivedFrom":subQ1}),1.0]])]});}
            var Q25;
            {var subQ3=sQuery(id+"F0.wireOp",EDGE,"E14");var subQ5=makeQuery(id+"F0.imprint","INTERSECT",VERTEX,{"derivedFrom":[sQuery(id+"F0.wireOp",EDGE,"E3.0"),subQ3]});Q25=makeQuery(id+"F0.imprint","IMPRINT",FACE,{"disambiguationData":[TD([[makeQuery(id+"F0.imprint","IMPRINT",EDGE,{"disambiguationData":[TD([[subQ5,1.0]])],"derivedFrom":subQ3}),1.0]])]});}
            var Q26;
            {var subQ1=sQuery(id+"F0.wireOp",EDGE,"E5.trimOffspring");Q26=makeQuery(id+"F0.imprint","IMPRINT",FACE,{"disambiguationData":[TD([[makeQuery(id+"F0.imprint","IMPRINT",EDGE,{"derivedFrom":subQ1}),-1.0]])]});}
            var Q27;
            {var subQ0=sQuery(id+"F0.wireOp",EDGE,"E68");Q27=makeQuery(id+"F0.imprint","IMPRINT",FACE,{"disambiguationData":[TD([[makeQuery(id+"F0.imprint","IMPRINT",EDGE,{"derivedFrom":subQ0}),1.0]])]});}
            var Q28;
            {var subQ8=sQuery(id+"F0.wireOp",EDGE,"E1.left");var subQ10=sQuery(id+"F0.wireOp",EDGE,"E6.trimOffspring");var subQ11=makeQuery(id+"F0.imprint","INTERSECT",VERTEX,{"derivedFrom":[subQ8,subQ10]});Q28=makeQuery(id+"F0.imprint","IMPRINT",FACE,{"disambiguationData":[TD([[makeQuery(id+"F0.imprint","IMPRINT",EDGE,{"disambiguationData":[TD([[subQ11,1.0]])],"derivedFrom":subQ8}),-1.0]])]});}
            var Q29;
            {var subQ7=sQuery(id+"F0.wireOp",EDGE,"E7.trimOffspring");var subQ8=sQuery(id+"F0.wireOp",EDGE,"E1.top");var subQ9=makeQuery(id+"F0.imprint","INTERSECT",VERTEX,{"derivedFrom":[subQ8,subQ7]});Q29=makeQuery(id+"F0.imprint","IMPRINT",FACE,{"disambiguationData":[TD([[makeQuery(id+"F0.imprint","IMPRINT",EDGE,{"disambiguationData":[TD([[subQ9,1.0]])],"derivedFrom":subQ8}),-1.0]])]});}
            var Q30;
            {var subQ0=sQuery(id+"F0.wireOp",EDGE,"E54");var subQ3=sQuery(id+"F0.wireOp",EDGE,"E32");var subQ4=makeQuery(id+"F0.imprint","INTERSECT",VERTEX,{"derivedFrom":[subQ3,subQ0]});Q30=makeQuery(id+"F0.imprint","IMPRINT",FACE,{"disambiguationData":[TD([[makeQuery(id+"F0.imprint","IMPRINT",EDGE,{"disambiguationData":[TD([[subQ4,-1.0]])],"derivedFrom":subQ3}),-1.0]])]});}
            var Q31;
            {var subQ0=sQuery(id+"F0.wireOp",EDGE,"E56");var subQ5=sQuery(id+"F0.wireOp",EDGE,"E32");var subQ6=makeQuery(id+"F0.imprint","INTERSECT",VERTEX,{"derivedFrom":[subQ5,subQ0]});Q31=makeQuery(id+"F0.imprint","IMPRINT",FACE,{"disambiguationData":[TD([[makeQuery(id+"F0.imprint","IMPRINT",EDGE,{"disambiguationData":[TD([[subQ6,-1.0]])],"derivedFrom":subQ5}),-1.0]])]});}
            var Q32;
            {var subQ3=sQuery(id+"F0.wireOp",EDGE,"E59");var subQ5=sQuery(id+"F0.wireOp",EDGE,"E28");var subQ7=makeQuery(id+"F0.imprint","INTERSECT",VERTEX,{"derivedFrom":[subQ5,subQ3]});Q32=makeQuery(id+"F0.imprint","IMPRINT",FACE,{"disambiguationData":[TD([[makeQuery(id+"F0.imprint","IMPRINT",EDGE,{"disambiguationData":[TD([[subQ7,-1.0]])],"derivedFrom":subQ5}),-1.0]])]});}
            var Q33;
            {var subQ0=sQuery(id+"F0.wireOp",EDGE,"E49");var subQ1=sQuery(id+"F0.wireOp",EDGE,"E29");var subQ2=makeQuery(id+"F0.imprint","INTERSECT",VERTEX,{"derivedFrom":[subQ1,subQ0]});Q33=makeQuery(id+"F0.imprint","IMPRINT",FACE,{"disambiguationData":[TD([[makeQuery(id+"F0.imprint","IMPRINT",EDGE,{"disambiguationData":[TD([[subQ2,-1.0]])],"derivedFrom":subQ1}),1.0]])]});}
            var Q34;
            {var subQ5=sQuery(id+"F0.wireOp",EDGE,"E49");var subQ7=sQuery(id+"F0.wireOp",EDGE,"E30");var subQ8=makeQuery(id+"F0.imprint","INTERSECT",VERTEX,{"derivedFrom":[subQ7,subQ5]});Q34=makeQuery(id+"F0.imprint","IMPRINT",FACE,{"disambiguationData":[TD([[makeQuery(id+"F0.imprint","IMPRINT",EDGE,{"disambiguationData":[TD([[subQ8,-1.0]])],"derivedFrom":subQ7}),1.0]])]});}
            var Q35;
            {var subQ1=sQuery(id+"F0.wireOp",EDGE,"E14");var subQ6=sQuery(id+"F0.wireOp",EDGE,"E2.0");var subQ8=makeQuery(id+"F0.imprint","INTERSECT",VERTEX,{"derivedFrom":[subQ6,subQ1]});Q35=makeQuery(id+"F0.imprint","IMPRINT",FACE,{"disambiguationData":[TD([[makeQuery(id+"F0.imprint","IMPRINT",EDGE,{"disambiguationData":[TD([[subQ8,-1.0]])],"derivedFrom":subQ1}),-1.0]])]});}
            var Q36;
            {var subQ2=sQuery(id+"F0.wireOp",EDGE,"E14");var subQ4=makeQuery(id+"F0.imprint","INTERSECT",VERTEX,{"derivedFrom":[sQuery(id+"F0.wireOp",EDGE,"E2.0"),subQ2]});Q36=makeQuery(id+"F0.imprint","IMPRINT",FACE,{"disambiguationData":[TD([[makeQuery(id+"F0.imprint","IMPRINT",EDGE,{"disambiguationData":[TD([[subQ4,1.0]])],"derivedFrom":subQ2}),1.0]])]});}
            var Q37;
            {var subQ0=sQuery(id+"F0.wireOp",EDGE,"E38");Q37=makeQuery(id+"F0.imprint","IMPRINT",FACE,{"disambiguationData":[TD([[makeQuery(id+"F0.imprint","IMPRINT",EDGE,{"derivedFrom":subQ0}),-1.0]])]});}
            extrude(context, id + "F2", {"entities" : qUnion([Q0, Q1, Q2, Q3, Q4, Q5, Q6, Q7, Q8, Q9, Q10, Q11, Q12, Q13, Q14, Q15, Q16, Q17, Q18, Q19, Q20, Q21, Q22, Q23, Q24, Q25, Q26, Q27, Q28, Q29, Q30, Q31, Q32, Q33, Q34, Q35, Q36, Q37]), "depth" : .35 * mm, "offsetDistance" : 25 * mm});
        }
    });
